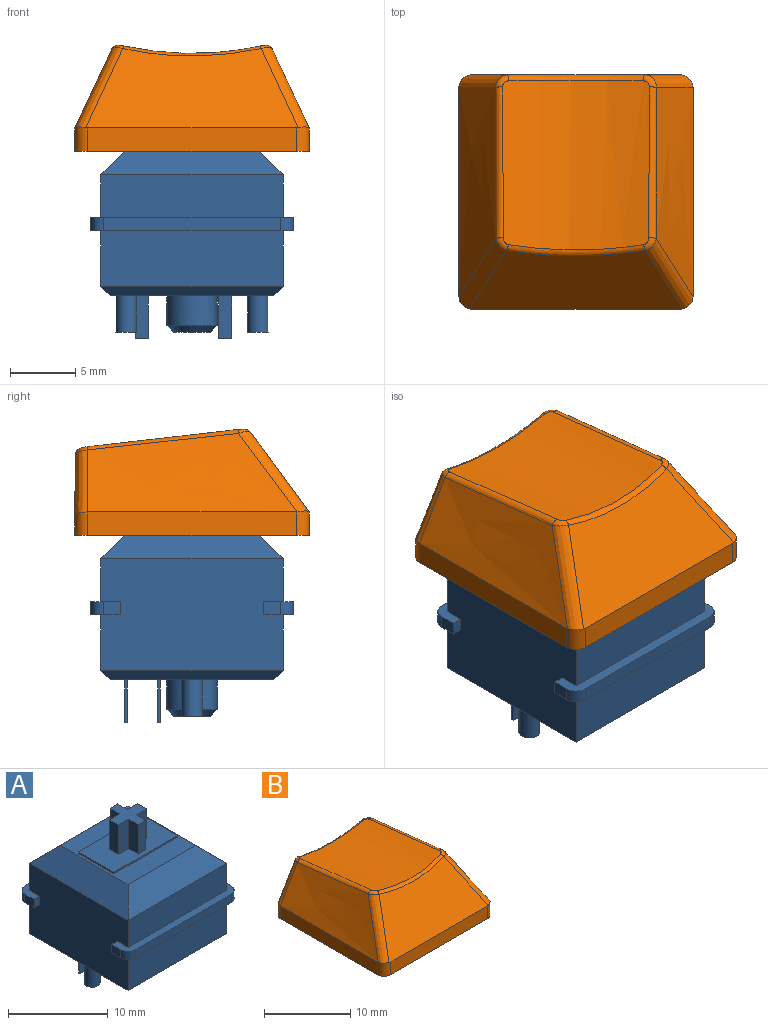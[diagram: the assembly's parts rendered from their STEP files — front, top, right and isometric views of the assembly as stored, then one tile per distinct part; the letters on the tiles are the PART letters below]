
ASSEMBLY  parts=2 mates=1
PART A: 69 faces, bbox 15.6x15.6x18.6 mm
  f0: plane 15.6x2.3mm, normal (0,0,-1), area 14.4mm2, adj f2,f3,f28,f30,f35,f60,f62,f63
  f1: plane 15.6x2.3mm, normal (0,0,-1), area 14.4mm2, adj f28,f30,f33,f34,f36,f59,f61,f64
  f2: plane 1.3x1mm, normal (1,0,0), area 1.3mm2, adj f0,f32,f62,f66
  f3: plane 1.3x1mm, normal (-1,0,0), area 1.3mm2, adj f0,f32,f63,f68
  f4: plane 15.6x2.3mm, normal (0,0,1), area 14.4mm2, adj f28,f30,f31,f33,f34,f36,f61,f64
  f5: plane 14x2.2mm, normal (-0.71,0,0.71), area 36.7mm2, adj f6,f7,f26,f30
  f6: plane 14x2.2mm, normal (0,-0.71,0.71), area 36.7mm2, adj f5,f7,f27,f31
  f7: plane 9.6x9.6mm, normal (0,0,1), area 47.2mm2, adj f5,f6,f8,f9,f10,f11,f26,f27
  f8: plane 5x0.2mm, normal (1,0,0), area 1mm2, adj f7,f9,f11,f12
  f9: plane 9x0.2mm, normal (0,1,0), area 1.8mm2, adj f7,f8,f10,f12
  f10: plane 5x0.2mm, normal (-1,0,0), area 1mm2, adj f7,f9,f11,f12
  f11: plane 9x0.2mm, normal (0,-1,0), area 1.8mm2, adj f7,f8,f10,f12
  f12: plane 9x5mm, normal (0,0,1), area 36.9mm2, adj f8,f9,f10,f11,f13,f14,f15,f16
  f13: plane 3.6x1.35mm, normal (1,0,0), area 4.9mm2, adj f12,f14,f24,f25
  f14: plane 3.6x1.08mm, normal (0,1,0), area 3.9mm2, adj f12,f13,f15,f25
  f15: plane 3.6x1.35mm, normal (-1,0,0), area 4.9mm2, adj f12,f14,f16,f25
  f16: plane 3.6x1.46mm, normal (0,1,0), area 5.3mm2, adj f12,f15,f17,f25
  f17: plane 3.6x1.3mm, normal (-1,0,0), area 4.7mm2, adj f12,f16,f18,f25
  f18: plane 3.6x1.46mm, normal (0,-1,0), area 5.3mm2, adj f12,f17,f19,f25
  f19: plane 3.6x1.35mm, normal (-1,0,0), area 4.9mm2, adj f12,f18,f20,f25
  f20: plane 3.6x1.08mm, normal (0,-1,0), area 3.9mm2, adj f12,f19,f21,f25
  f21: plane 3.6x1.35mm, normal (1,0,0), area 4.9mm2, adj f12,f20,f22,f25
  f22: plane 3.6x1.46mm, normal (0,-1,0), area 5.3mm2, adj f12,f21,f23,f25
  f23: plane 3.6x1.3mm, normal (1,0,0), area 4.7mm2, adj f12,f22,f24,f25
  f24: plane 3.6x1.46mm, normal (0,1,0), area 5.3mm2, adj f12,f13,f23,f25
  f25: plane 4x4mm, normal (0,0,1), area 8.1mm2, adj f13,f14,f15,f16,f17,f18,f19,f20
  f26: plane 14x2.2mm, normal (0,0.71,0.71), area 36.7mm2, adj f5,f7,f27,f29
  f27: plane 14x2.2mm, normal (0.71,0,0.71), area 36.7mm2, adj f6,f7,f26,f28
  f28: plane 14x8.6mm, normal (1,0,0), area 117.4mm2, adj f0,f1,f4,f27,f29,f31,f32,f55
  f29: plane 14x3.3mm, normal (0,1,0), area 46.2mm2, adj f26,f28,f30,f32
  f30: plane 14x8.6mm, normal (-1,0,0), area 117.4mm2, adj f0,f1,f4,f5,f29,f31,f32,f57
  f31: plane 14x3.3mm, normal (0,-1,0), area 46.2mm2, adj f4,f6,f28,f30
  f32: plane 15.6x2.3mm, normal (0,0,1), area 14.4mm2, adj f2,f3,f28,f29,f30,f35,f62,f63
  f33: plane 13.6x1mm, normal (0,-1,0), area 13.6mm2, adj f1,f4,f61,f64
  f34: plane 1.3x1mm, normal (1,0,0), area 1.3mm2, adj f1,f4,f61,f65
  f35: plane 13.6x1mm, normal (0,1,0), area 13.6mm2, adj f0,f32,f62,f63
  f36: plane 1.3x1mm, normal (-1,0,0), area 1.3mm2, adj f1,f4,f64,f67
  f37: plane 2.85x2.85mm, normal (0,0,-1), area 6.4mm2, adj f38
  f38: cone r=1.43mm half-angle=45deg, axis (0,0,1), area 7.4mm2, adj f37,f43
  f39: plane 1x0.2mm, normal (0,0,-1), area 0.2mm2, adj f44,f45,f46,f47
  f40: plane 1x0.2mm, normal (0,0,-1), area 0.2mm2, adj f48,f49,f50,f51
  f41: plane 1.6x1.6mm, normal (0,0,-1), area 2mm2, adj f52
  f42: plane 1.6x1.6mm, normal (0,0,-1), area 2mm2, adj f53
  f43: cylinder r=1.93mm len=3.85mm, axis (0,0,1), area 27.8mm2, adj f38,f54
  f44: plane 3.3x0.2mm, normal (-1,0,0), area 0.7mm2, adj f39,f45,f47,f54
  f45: plane 3.3x1mm, normal (0,1,0), area 3.3mm2, adj f39,f44,f46,f54
  f46: plane 3.3x0.2mm, normal (1,0,0), area 0.7mm2, adj f39,f45,f47,f54
  f47: plane 3.3x1mm, normal (0,-1,0), area 3.3mm2, adj f39,f44,f46,f54
  f48: plane 3.3x0.2mm, normal (-1,0,0), area 0.7mm2, adj f40,f49,f51,f54
  f49: plane 3.3x1mm, normal (0,1,0), area 3.3mm2, adj f40,f48,f50,f54
  f50: plane 3.3x0.2mm, normal (1,0,0), area 0.7mm2, adj f40,f49,f51,f54
  f51: plane 3.3x1mm, normal (0,-1,0), area 3.3mm2, adj f40,f48,f50,f54
  f52: cylinder r=0.8mm len=2.8mm, axis (0,0,1), area 14.1mm2, adj f41,f54
  f53: cylinder r=0.8mm len=2.8mm, axis (0,0,1), area 14.1mm2, adj f42,f54
  f54: plane 12.6x12.6mm, normal (0,0,-1), area 142.7mm2, adj f43,f44,f45,f46,f47,f48,f49,f50
  f55: plane 14x0.7mm, normal (0.71,0,-0.71), area 13.2mm2, adj f28,f54,f56,f58
  f56: plane 14x0.7mm, normal (0,0.71,-0.71), area 13.2mm2, adj f54,f55,f57,f60
  f57: plane 14x0.7mm, normal (-0.71,0,-0.71), area 13.2mm2, adj f30,f54,f56,f58
  f58: plane 14x0.7mm, normal (0,-0.71,-0.71), area 13.2mm2, adj f54,f55,f57,f59
  f59: plane 14x4.3mm, normal (0,-1,0), area 60.2mm2, adj f1,f28,f30,f58
  f60: plane 14x4.3mm, normal (0,1,0), area 60.2mm2, adj f0,f28,f30,f56
  f61: cylinder r=1mm len=1mm, axis (0,0,-1), area 1.6mm2, adj f1,f4,f33,f34
  f62: cylinder r=1mm len=1mm, axis (0,0,1), area 1.6mm2, adj f0,f2,f32,f35
  f63: cylinder r=1mm len=1mm, axis (0,0,-1), area 1.6mm2, adj f0,f3,f32,f35
  f64: cylinder r=1mm len=1mm, axis (0,0,1), area 1.6mm2, adj f1,f4,f33,f36
  f65: plane 1x0.8mm, normal (0,1,0), area 0.8mm2, adj f1,f4,f28,f34
  f66: plane 1x0.8mm, normal (0,-1,0), area 0.8mm2, adj f0,f2,f28,f32
  f67: plane 1x0.8mm, normal (0,1,0), area 0.8mm2, adj f1,f4,f30,f36
  f68: plane 1x0.8mm, normal (0,-1,0), area 0.8mm2, adj f0,f3,f30,f32
PART B: 50 faces, bbox 21.2x22.7x10.6 mm
  f0: plane 18x18mm, normal (0,0,-1), area 67.1mm2, adj f1,f2,f3,f4,f10,f12,f14,f16
  f1: plane 16x1.8mm, normal (1,0,0), area 28.8mm2, adj f0,f8,f10,f16
  f2: plane 16.02x1.82mm, normal (0,1,0), area 28.8mm2, adj f0,f5,f14,f15,f16,f17
  f3: plane 16x1.8mm, normal (-1,0,0), area 28.8mm2, adj f0,f6,f12,f14
  f4: plane 16x1.8mm, normal (0,-1,0), area 28.8mm2, adj f0,f7,f10,f12
  f5: plane 15.68x4.35mm, normal (0,1,0), area 52.7mm2, adj f2,f15,f17,f20
  f6: bspline ~18x6.51mm, area 85.6mm2, adj f3,f12,f13,f15,f19
  f7: plane 16.34x6.11mm, normal (0,-0.81,0.59), area 97.2mm2, adj f4,f10,f11,f12,f13,f23
  f8: bspline ~18x6.51mm, area 85.6mm2, adj f1,f10,f11,f17,f24
  f9: cylinder r=22.9mm len=13.02mm, axis (0,0.99,-0.11), area 145.8mm2, adj f18,f19,f20,f21,f22,f23,f24,f25
  f10: cylinder r=1mm len=1.88mm, axis (0,0,-1), area 2.9mm2, adj f0,f1,f4,f7,f8,f11
  f11: bspline ~8.07x6.49mm, area 10.8mm2, adj f7,f8,f10,f25
  f12: cylinder r=1mm len=1.88mm, axis (0,0,1), area 2.9mm2, adj f0,f3,f4,f6,f7,f13
  f13: bspline ~8.08x6.5mm, area 10.8mm2, adj f6,f7,f12,f21
  f14: cylinder r=1mm len=1.8mm, axis (0,0,-1), area 2.7mm2, adj f0,f2,f3,f15
  f15: bspline ~6.93x4.65mm, area 8.3mm2, adj f2,f5,f6,f14,f18
  f16: cylinder r=1mm len=1.8mm, axis (0,0,1), area 2.7mm2, adj f0,f1,f2,f17
  f17: bspline ~6.92x4.64mm, area 8.3mm2, adj f2,f5,f8,f16,f22
  f18: bspline ~1.17x1.07mm, area 0.8mm2, adj f9,f15,f19,f20
  f19: bspline ~17.39x2.3mm, area 7.9mm2, adj f6,f9,f18,f21
  f20: bspline ~10.57x1.09mm, area 7.6mm2, adj f5,f9,f18,f22
  f21: bspline ~1.3x1.11mm, area 0.6mm2, adj f9,f13,f19,f23
  f22: bspline ~1.23x1.01mm, area 0.8mm2, adj f9,f17,f20,f24
  f23: bspline ~10.63x0.88mm, area 5.6mm2, adj f7,f9,f21,f25
  f24: bspline ~17.39x2.3mm, area 7.9mm2, adj f8,f9,f22,f25
  f25: bspline ~1.3x1.11mm, area 0.6mm2, adj f9,f11,f23,f24
  f26: plane 16.04x1.61mm, normal (-1,0,0), area 24.9mm2, adj f0,f27,f29,f32,f33
  f27: plane 16x1.8mm, normal (0,-1,0), area 28.7mm2, adj f0,f26,f28,f30,f31,f33
  f28: plane 16.04x1.61mm, normal (1,0,0), area 24.9mm2, adj f0,f27,f29,f31,f32
  f29: plane 16x1.47mm, normal (0,1,0), area 23.6mm2, adj f0,f26,f28,f32
  f30: plane 15.83x4.1mm, normal (0,-1,0), area 47.9mm2, adj f27,f31,f33,f34
  f31: offset ~20x8.51mm, area 77.3mm2, adj f27,f28,f30,f32,f34
  f32: plane 16.71x6.33mm, normal (0,0.81,-0.59), area 88.7mm2, adj f26,f28,f29,f31,f33,f34
  f33: offset ~20x8.51mm, area 77.3mm2, adj f26,f27,f30,f32,f34
  f34: cylinder r=23.9mm len=11.93mm, axis (0,0.99,-0.11), area 107.8mm2, adj f30,f31,f32,f33,f46
  f35: plane 5.35x1.5mm, normal (-1,0,0), area 7.9mm2, adj f36,f44,f45,f49
  f36: plane 5.44x1.5mm, normal (0,-1,0), area 8.1mm2, adj f35,f37,f45,f49
  f37: plane 5.58x1.3mm, normal (-1,0,0), area 7.2mm2, adj f36,f38,f45,f49
  f38: plane 5.59x1.5mm, normal (0,1,0), area 8.3mm2, adj f37,f39,f45,f49
  f39: plane 5.67x1.5mm, normal (-1,0,0), area 8.4mm2, adj f38,f40,f45,f49
  f40: plane 5.67x1.3mm, normal (0,1,0), area 7.4mm2, adj f39,f41,f45,f49
  f41: plane 5.67x1.5mm, normal (1,0,0), area 8.4mm2, adj f40,f42,f45,f49
  f42: plane 5.59x1.5mm, normal (0,1,0), area 8.3mm2, adj f41,f43,f45,f49
  f43: plane 5.58x1.3mm, normal (1,0,0), area 7.2mm2, adj f42,f45,f47,f49
  f44: plane 5.17x1.3mm, normal (0,-1,0), area 6.7mm2, adj f35,f45,f48,f49
  f45: plane 5.5x5.5mm, normal (0,0,-1), area 14.3mm2, adj f35,f36,f37,f38,f39,f40,f41,f42
  f46: cylinder r=2.75mm len=5.57mm, axis (0,0,-1), area 96.3mm2, adj f34,f45
  f47: plane 5.44x1.5mm, normal (0,-1,0), area 8.1mm2, adj f43,f45,f48,f49
  f48: plane 5.35x1.5mm, normal (1,0,0), area 7.9mm2, adj f44,f45,f47,f49
  f49: cylinder r=23.9mm len=4.31mm, axis (0,0.99,-0.11), area 9.6mm2, adj f35,f36,f37,f38,f39,f40,f41,f42
PLACE A at identity fixed
PLACE B t=(0,0,11.1)mm
MATE fastened A.f38 <-> B.f46  axis (0,0,1) through (0,0,11.7)mm
